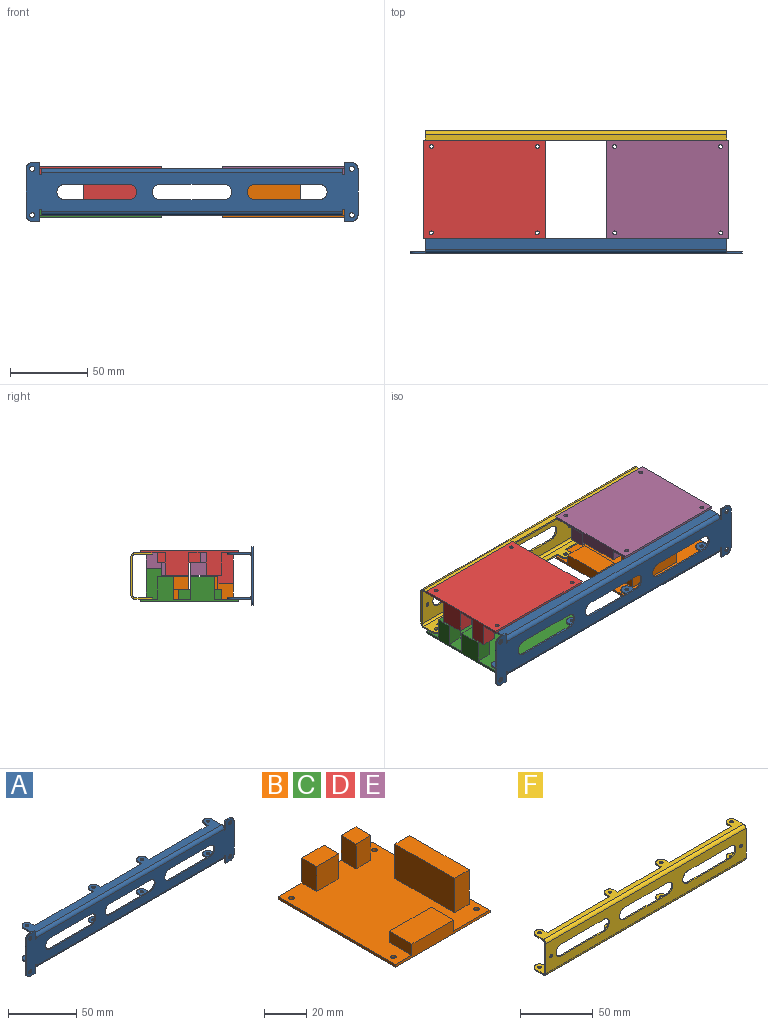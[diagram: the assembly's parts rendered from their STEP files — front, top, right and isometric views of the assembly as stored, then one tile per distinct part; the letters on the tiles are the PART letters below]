
ASSEMBLY  parts=6 mates=5
PART A: 90 faces, bbox 214.8x16.8x38 mm
  f0: plane 214.76x38mm, normal (0,-1,0), area 4067.3mm2, adj f2,f3,f4,f5,f6,f7,f8,f9
  f1: plane 214.76x38mm, normal (0,1,0), area 4067.3mm2, adj f2,f3,f4,f5,f6,f7,f8,f9
  f2: plane 41.59x1mm, normal (0,0,1), area 41.6mm2, adj f0,f1,f29,f31
  f3: plane 41.59x1mm, normal (0,0,-1), area 41.6mm2, adj f0,f1,f24,f30
  f4: plane 7.25x1mm, normal (-1,0,0), area 7.2mm2, adj f0,f1,f5,f34
  f5: plane 4.94x1mm, normal (0,0,-1), area 4.9mm2, adj f0,f1,f4,f25
  f6: plane 30x1mm, normal (1,0,0), area 30mm2, adj f0,f1,f22,f25
  f7: plane 4.94x1mm, normal (0,0,1), area 4.9mm2, adj f0,f1,f8,f22
  f8: plane 7.25x1mm, normal (-1,0,0), area 7.2mm2, adj f0,f1,f7,f37
  f9: plane 7.25x1mm, normal (1,0,0), area 7.2mm2, adj f0,f1,f10,f38
  f10: plane 4.94x1mm, normal (0,0,1), area 4.9mm2, adj f0,f1,f9,f27
  f11: plane 30x1mm, normal (-1,0,0), area 30mm2, adj f0,f1,f26,f27
  f12: plane 4.94x1mm, normal (0,0,-1), area 4.9mm2, adj f0,f1,f19,f26
  f13: plane 41.59x1mm, normal (0,0,-1), area 41.6mm2, adj f0,f1,f23,f28
  f14: plane 41.59x1mm, normal (0,0,1), area 41.6mm2, adj f0,f1,f23,f28
  f15: cylinder r=1.6mm len=3.2mm, axis (0,1,0), area 10.1mm2, adj f0,f1
  f16: cylinder r=1.6mm len=3.2mm, axis (0,1,0), area 10.1mm2, adj f0,f1
  f17: cylinder r=1.6mm len=3.2mm, axis (0,1,0), area 10.1mm2, adj f0,f1
  f18: cylinder r=1.6mm len=3.2mm, axis (0,1,0), area 10.1mm2, adj f0,f1
  f19: plane 7.25x1mm, normal (1,0,0), area 7.2mm2, adj f0,f1,f12,f33
  f20: plane 41.59x1mm, normal (0,0,1), area 41.6mm2, adj f0,f1,f24,f30
  f21: plane 41.59x1mm, normal (0,0,-1), area 41.6mm2, adj f0,f1,f29,f31
  f22: cylinder r=4mm len=4mm, axis (0,-1,0), area 6.3mm2, adj f0,f1,f6,f7
  f23: cylinder r=5mm len=10mm, axis (0,1,0), area 15.7mm2, adj f0,f1,f13,f14
  f24: cylinder r=5mm len=10mm, axis (0,-1,0), area 15.7mm2, adj f0,f1,f3,f20
  f25: cylinder r=4mm len=4mm, axis (0,1,0), area 6.3mm2, adj f0,f1,f5,f6
  f26: cylinder r=4mm len=4mm, axis (0,1,0), area 6.3mm2, adj f0,f1,f11,f12
  f27: cylinder r=4mm len=4mm, axis (0,-1,0), area 6.3mm2, adj f0,f1,f10,f11
  f28: cylinder r=5mm len=10mm, axis (0,1,0), area 15.7mm2, adj f0,f1,f13,f14
  f29: cylinder r=5mm len=10mm, axis (0,-1,0), area 15.7mm2, adj f0,f1,f2,f21
  f30: cylinder r=5mm len=10mm, axis (0,1,0), area 15.7mm2, adj f0,f1,f3,f20
  f31: cylinder r=5mm len=10mm, axis (0,-1,0), area 15.7mm2, adj f0,f1,f2,f21
  f32: plane 1x0.75mm, normal (-1,0,0), area 0.7mm2, adj f0,f1,f33,f62
  f33: cylinder r=0.53mm len=1.06mm, axis (0,1,0), area 1.7mm2, adj f0,f1,f19,f32
  f34: cylinder r=0.53mm len=1.06mm, axis (0,1,0), area 1.7mm2, adj f0,f1,f4,f35
  f35: plane 1x0.75mm, normal (1,0,0), area 0.7mm2, adj f0,f1,f34,f61
  f36: plane 1x0.75mm, normal (1,0,0), area 0.7mm2, adj f0,f1,f37,f86
  f37: cylinder r=0.53mm len=1.06mm, axis (0,1,0), area 1.7mm2, adj f0,f1,f8,f36
  f38: cylinder r=0.53mm len=1.06mm, axis (0,1,0), area 1.7mm2, adj f0,f1,f9,f39
  f39: plane 1x0.75mm, normal (-1,0,0), area 0.7mm2, adj f0,f1,f38,f87
  f40: cylinder r=3.8mm len=7.6mm, axis (0,0,-1), area 11.9mm2, adj f41,f58,f59,f60
  f41: plane 3.8x1mm, normal (1,0,0), area 3.8mm2, adj f40,f42,f59,f60
  f42: plane 60.98x1mm, normal (0,1,0), area 61mm2, adj f41,f43,f59,f60
  f43: plane 3.8x1mm, normal (-1,0,0), area 3.8mm2, adj f42,f44,f59,f60
  f44: cylinder r=3.8mm len=7.6mm, axis (0,0,-1), area 11.9mm2, adj f43,f45,f59,f60
  f45: plane 3.8x1mm, normal (1,0,0), area 3.8mm2, adj f44,f46,f59,f60
  f46: plane 42.4x1mm, normal (0,1,0), area 42.4mm2, adj f45,f47,f59,f60
  f47: plane 3.8x1mm, normal (-1,0,0), area 3.8mm2, adj f46,f48,f59,f60
  f48: cylinder r=3.8mm len=7.6mm, axis (0,0,-1), area 11.9mm2, adj f47,f49,f59,f60
  f49: plane 3.8x1mm, normal (1,0,0), area 3.8mm2, adj f48,f50,f59,f60
  f50: plane 60.98x1mm, normal (0,1,0), area 61mm2, adj f49,f51,f59,f60
  f51: plane 3.8x1mm, normal (-1,0,0), area 3.8mm2, adj f50,f52,f59,f60
  f52: cylinder r=3.8mm len=7.6mm, axis (0,0,-1), area 11.9mm2, adj f51,f53,f59,f60
  f53: plane 10.5x1mm, normal (1,0,0), area 10.5mm2, adj f52,f59,f60,f61
  f54: cylinder r=1.25mm len=2.5mm, axis (0,0,-1), area 7.9mm2, adj f59,f60
  f55: cylinder r=1.25mm len=2.5mm, axis (0,0,-1), area 7.9mm2, adj f59,f60
  f56: cylinder r=1.25mm len=2.5mm, axis (0,0,-1), area 7.9mm2, adj f59,f60
  f57: cylinder r=1.25mm len=2.5mm, axis (0,0,-1), area 7.9mm2, adj f59,f60
  f58: plane 10.5x1mm, normal (-1,0,0), area 10.5mm2, adj f40,f59,f60,f62
  f59: plane 194.76x14.3mm, normal (0,0,-1), area 1491.5mm2, adj f40,f41,f42,f43,f44,f45,f46,f47
  f60: plane 194.76x14.3mm, normal (0,0,1), area 1491.5mm2, adj f40,f41,f42,f43,f44,f45,f46,f47
  f61: plane 2.5x2.5mm, normal (1,0,0), area 3.1mm2, adj f35,f53,f63,f64
  f62: plane 2.5x2.5mm, normal (-1,0,0), area 3.1mm2, adj f32,f58,f63,f64
  f63: cylinder r=2.5mm len=194.76mm, axis (1,0,0), area 764.8mm2, adj f0,f59,f61,f62
  f64: cylinder r=1.5mm len=194.76mm, axis (1,0,0), area 458.9mm2, adj f1,f60,f61,f62
  f65: cylinder r=3.8mm len=7.6mm, axis (0,0,1), area 11.9mm2, adj f66,f83,f84,f85
  f66: plane 3.8x1mm, normal (-1,0,0), area 3.8mm2, adj f65,f67,f84,f85
  f67: plane 60.98x1mm, normal (0,1,0), area 61mm2, adj f66,f68,f84,f85
  f68: plane 3.8x1mm, normal (1,0,0), area 3.8mm2, adj f67,f69,f84,f85
  f69: cylinder r=3.8mm len=7.6mm, axis (0,0,1), area 11.9mm2, adj f68,f70,f84,f85
  f70: plane 3.8x1mm, normal (-1,0,0), area 3.8mm2, adj f69,f71,f84,f85
  f71: plane 42.4x1mm, normal (0,1,0), area 42.4mm2, adj f70,f72,f84,f85
  f72: plane 3.8x1mm, normal (1,0,0), area 3.8mm2, adj f71,f73,f84,f85
  f73: cylinder r=3.8mm len=7.6mm, axis (0,0,1), area 11.9mm2, adj f72,f74,f84,f85
  f74: plane 3.8x1mm, normal (-1,0,0), area 3.8mm2, adj f73,f75,f84,f85
  f75: plane 60.98x1mm, normal (0,1,0), area 61mm2, adj f74,f76,f84,f85
  f76: plane 3.8x1mm, normal (1,0,0), area 3.8mm2, adj f75,f77,f84,f85
  f77: cylinder r=3.8mm len=7.6mm, axis (0,0,1), area 11.9mm2, adj f76,f78,f84,f85
  f78: plane 10.5x1mm, normal (-1,0,0), area 10.5mm2, adj f77,f84,f85,f87
  f79: cylinder r=1.25mm len=2.5mm, axis (0,0,1), area 7.9mm2, adj f84,f85
  f80: cylinder r=1.25mm len=2.5mm, axis (0,0,1), area 7.9mm2, adj f84,f85
  f81: cylinder r=1.25mm len=2.5mm, axis (0,0,1), area 7.9mm2, adj f84,f85
  f82: cylinder r=1.25mm len=2.5mm, axis (0,0,1), area 7.9mm2, adj f84,f85
  f83: plane 10.5x1mm, normal (1,0,0), area 10.5mm2, adj f65,f84,f85,f86
  f84: plane 194.76x14.3mm, normal (0,0,1), area 1491.5mm2, adj f65,f66,f67,f68,f69,f70,f71,f72
  f85: plane 194.76x14.3mm, normal (0,0,-1), area 1491.5mm2, adj f65,f66,f67,f68,f69,f70,f71,f72
  f86: plane 2.5x2.5mm, normal (1,0,0), area 3.1mm2, adj f36,f83,f88,f89
  f87: plane 2.5x2.5mm, normal (-1,0,0), area 3.1mm2, adj f39,f78,f88,f89
  f88: cylinder r=2.5mm len=194.76mm, axis (1,0,0), area 764.8mm2, adj f0,f84,f86,f87
  f89: cylinder r=1.5mm len=194.76mm, axis (1,0,0), area 458.9mm2, adj f1,f85,f86,f87
PART B: 27 faces, bbox 63.5x79.1x21.5 mm
  f0: plane 79.12x63.5mm, normal (0,0,1), area 3934.5mm2, adj f1,f2,f3,f4,f6,f7,f8,f9
  f1: plane 63.5x8mm, normal (0,-1,0), area 277.3mm2, adj f0,f2,f4,f5,f23,f24,f26
  f2: plane 79.12x1.5mm, normal (1,0,0), area 118.7mm2, adj f0,f1,f3,f5
  f3: plane 63.5x16mm, normal (0,1,0), area 457.7mm2, adj f0,f2,f4,f5,f10,f12,f13,f14
  f4: plane 79.12x1.5mm, normal (-1,0,0), area 118.7mm2, adj f0,f1,f3,f5
  f5: plane 79.12x63.5mm, normal (0,0,-1), area 5004.5mm2, adj f1,f2,f3,f4,f6,f7,f8,f9
  f6: cylinder r=1.25mm len=2.5mm, axis (0,0,1), area 11.8mm2, adj f0,f5
  f7: cylinder r=1.25mm len=2.5mm, axis (0,0,1), area 11.8mm2, adj f0,f5
  f8: cylinder r=1.25mm len=2.5mm, axis (0,0,1), area 11.8mm2, adj f0,f5
  f9: cylinder r=1.25mm len=2.5mm, axis (0,0,1), area 11.8mm2, adj f0,f5
  f10: plane 14.5x10mm, normal (-1,0,0), area 145mm2, adj f0,f3,f11,f13
  f11: plane 15x14.5mm, normal (0,-1,0), area 217.5mm2, adj f0,f10,f12,f13
  f12: plane 14.5x10mm, normal (1,0,0), area 145mm2, adj f0,f3,f11,f13
  f13: plane 15x10mm, normal (0,0,1), area 150mm2, adj f3,f10,f11,f12
  f14: plane 14.5x10mm, normal (1,0,0), area 145mm2, adj f0,f3,f16,f17
  f15: plane 14.5x10mm, normal (-1,0,0), area 145mm2, adj f0,f3,f16,f17
  f16: plane 14.5x10mm, normal (0,-1,0), area 145mm2, adj f0,f14,f15,f17
  f17: plane 10x10mm, normal (0,0,1), area 100mm2, adj f3,f14,f15,f16
  f18: plane 20x10mm, normal (0,1,0), area 200mm2, adj f0,f19,f21,f22
  f19: plane 40x20mm, normal (-1,0,0), area 800mm2, adj f0,f18,f20,f22
  f20: plane 20x10mm, normal (0,-1,0), area 200mm2, adj f0,f19,f21,f22
  f21: plane 40x20mm, normal (1,0,0), area 800mm2, adj f0,f18,f20,f22
  f22: plane 40x10mm, normal (0,0,1), area 400mm2, adj f18,f19,f20,f21
  f23: plane 15x6.5mm, normal (-1,0,0), area 97.5mm2, adj f0,f1,f25,f26
  f24: plane 15x6.5mm, normal (1,0,0), area 97.5mm2, adj f0,f1,f25,f26
  f25: plane 28x6.5mm, normal (0,1,0), area 182mm2, adj f0,f23,f24,f26
  f26: plane 28x15mm, normal (0,0,1), area 420mm2, adj f1,f23,f24,f25
PART C: same geometry as B
PART D: same geometry as B
PART E: same geometry as B
PART F: 68 faces, bbox 194.8x13.9x30 mm
  f0: plane 41.59x1mm, normal (0,0,1), area 41.6mm2, adj f10,f11,f13,f17
  f1: plane 41.59x1mm, normal (0,0,-1), area 41.6mm2, adj f10,f11,f12,f16
  f2: plane 25x1mm, normal (-1,0,0), area 25mm2, adj f10,f11,f40,f65
  f3: plane 41.59x1mm, normal (0,0,-1), area 41.6mm2, adj f10,f11,f14,f15
  f4: plane 41.59x1mm, normal (0,0,1), area 41.6mm2, adj f10,f11,f14,f15
  f5: cylinder r=1.25mm len=2.5mm, axis (0,1,0), area 7.9mm2, adj f10,f11
  f6: cylinder r=1.25mm len=2.5mm, axis (0,1,0), area 7.9mm2, adj f10,f11
  f7: plane 25x1mm, normal (1,0,0), area 25mm2, adj f10,f11,f39,f64
  f8: plane 41.59x1mm, normal (0,0,1), area 41.6mm2, adj f10,f11,f12,f16
  f9: plane 41.59x1mm, normal (0,0,-1), area 41.6mm2, adj f10,f11,f13,f17
  f10: plane 194.76x25mm, normal (0,-1,0), area 3376mm2, adj f0,f1,f2,f3,f4,f5,f6,f7
  f11: plane 194.76x25mm, normal (0,1,0), area 3376mm2, adj f0,f1,f2,f3,f4,f5,f6,f7
  f12: cylinder r=5mm len=10mm, axis (0,-1,0), area 15.7mm2, adj f1,f8,f10,f11
  f13: cylinder r=5mm len=10mm, axis (0,-1,0), area 15.7mm2, adj f0,f9,f10,f11
  f14: cylinder r=5mm len=10mm, axis (0,-1,0), area 15.7mm2, adj f3,f4,f10,f11
  f15: cylinder r=5mm len=10mm, axis (0,-1,0), area 15.7mm2, adj f3,f4,f10,f11
  f16: cylinder r=5mm len=10mm, axis (0,-1,0), area 15.7mm2, adj f1,f8,f10,f11
  f17: cylinder r=5mm len=10mm, axis (0,1,0), area 15.7mm2, adj f0,f9,f10,f11
  f18: cylinder r=3.8mm len=7.6mm, axis (0,0,-1), area 11.9mm2, adj f19,f36,f37,f38
  f19: plane 3.8x1mm, normal (1,0,0), area 3.8mm2, adj f18,f20,f37,f38
  f20: plane 60.98x1mm, normal (0,1,0), area 61mm2, adj f19,f21,f37,f38
  f21: plane 3.8x1mm, normal (-1,0,0), area 3.8mm2, adj f20,f22,f37,f38
  f22: cylinder r=3.8mm len=7.6mm, axis (0,0,-1), area 11.9mm2, adj f21,f23,f37,f38
  f23: plane 3.8x1mm, normal (1,0,0), area 3.8mm2, adj f22,f24,f37,f38
  f24: plane 42.4x1mm, normal (0,1,0), area 42.4mm2, adj f23,f25,f37,f38
  f25: plane 3.8x1mm, normal (-1,0,0), area 3.8mm2, adj f24,f26,f37,f38
  f26: cylinder r=3.8mm len=7.6mm, axis (0,0,-1), area 11.9mm2, adj f25,f27,f37,f38
  f27: plane 3.8x1mm, normal (1,0,0), area 3.8mm2, adj f26,f28,f37,f38
  f28: plane 60.98x1mm, normal (0,1,0), area 61mm2, adj f27,f29,f37,f38
  f29: plane 3.8x1mm, normal (-1,0,0), area 3.8mm2, adj f28,f30,f37,f38
  f30: cylinder r=3.8mm len=7.6mm, axis (0,0,-1), area 11.9mm2, adj f29,f31,f37,f38
  f31: plane 7.62x1mm, normal (1,0,0), area 7.6mm2, adj f30,f37,f38,f39
  f32: cylinder r=1.25mm len=2.5mm, axis (0,0,-1), area 7.9mm2, adj f37,f38
  f33: cylinder r=1.25mm len=2.5mm, axis (0,0,-1), area 7.9mm2, adj f37,f38
  f34: cylinder r=1.25mm len=2.5mm, axis (0,0,-1), area 7.9mm2, adj f37,f38
  f35: cylinder r=1.25mm len=2.5mm, axis (0,0,-1), area 7.9mm2, adj f37,f38
  f36: plane 7.62x1mm, normal (-1,0,0), area 7.6mm2, adj f18,f37,f38,f40
  f37: plane 194.76x11.42mm, normal (0,0,-1), area 930.6mm2, adj f18,f19,f20,f21,f22,f23,f24,f25
  f38: plane 194.76x11.42mm, normal (0,0,1), area 930.6mm2, adj f18,f19,f20,f21,f22,f23,f24,f25
  f39: plane 2.5x2.5mm, normal (1,0,0), area 3.1mm2, adj f7,f31,f41,f42
  f40: plane 2.5x2.5mm, normal (-1,0,0), area 3.1mm2, adj f2,f36,f41,f42
  f41: cylinder r=2.5mm len=194.76mm, axis (1,0,0), area 764.8mm2, adj f10,f37,f39,f40
  f42: cylinder r=1.5mm len=194.76mm, axis (1,0,0), area 458.9mm2, adj f11,f38,f39,f40
  f43: cylinder r=3.8mm len=7.6mm, axis (0,0,1), area 11.9mm2, adj f44,f61,f62,f63
  f44: plane 3.8x1mm, normal (-1,0,0), area 3.8mm2, adj f43,f45,f62,f63
  f45: plane 60.98x1mm, normal (0,1,0), area 61mm2, adj f44,f46,f62,f63
  f46: plane 3.8x1mm, normal (1,0,0), area 3.8mm2, adj f45,f47,f62,f63
  f47: cylinder r=3.8mm len=7.6mm, axis (0,0,1), area 11.9mm2, adj f46,f48,f62,f63
  f48: plane 3.8x1mm, normal (-1,0,0), area 3.8mm2, adj f47,f49,f62,f63
  f49: plane 42.4x1mm, normal (0,1,0), area 42.4mm2, adj f48,f50,f62,f63
  f50: plane 3.8x1mm, normal (1,0,0), area 3.8mm2, adj f49,f51,f62,f63
  f51: cylinder r=3.8mm len=7.6mm, axis (0,0,1), area 11.9mm2, adj f50,f52,f62,f63
  f52: plane 3.8x1mm, normal (-1,0,0), area 3.8mm2, adj f51,f53,f62,f63
  f53: plane 60.98x1mm, normal (0,1,0), area 61mm2, adj f52,f54,f62,f63
  f54: plane 3.8x1mm, normal (1,0,0), area 3.8mm2, adj f53,f55,f62,f63
  f55: cylinder r=3.8mm len=7.6mm, axis (0,0,1), area 11.9mm2, adj f54,f56,f62,f63
  f56: plane 7.62x1mm, normal (-1,0,0), area 7.6mm2, adj f55,f62,f63,f65
  f57: cylinder r=1.25mm len=2.5mm, axis (0,0,1), area 7.9mm2, adj f62,f63
  f58: cylinder r=1.25mm len=2.5mm, axis (0,0,1), area 7.9mm2, adj f62,f63
  f59: cylinder r=1.25mm len=2.5mm, axis (0,0,1), area 7.9mm2, adj f62,f63
  f60: cylinder r=1.25mm len=2.5mm, axis (0,0,1), area 7.9mm2, adj f62,f63
  f61: plane 7.62x1mm, normal (1,0,0), area 7.6mm2, adj f43,f62,f63,f64
  f62: plane 194.76x11.42mm, normal (0,0,1), area 930.6mm2, adj f43,f44,f45,f46,f47,f48,f49,f50
  f63: plane 194.76x11.42mm, normal (0,0,-1), area 930.6mm2, adj f43,f44,f45,f46,f47,f48,f49,f50
  f64: plane 2.5x2.5mm, normal (1,0,0), area 3.1mm2, adj f7,f61,f66,f67
  f65: plane 2.5x2.5mm, normal (-1,0,0), area 3.1mm2, adj f2,f56,f66,f67
  f66: cylinder r=2.5mm len=194.76mm, axis (1,0,0), area 764.8mm2, adj f10,f62,f64,f65
  f67: cylinder r=1.5mm len=194.76mm, axis (1,0,0), area 458.9mm2, adj f11,f63,f64,f65
PLACE A at identity
PLACE B rot(axis=(0,0,-1),90deg) t=(59.29,0,20)mm
PLACE C rot(axis=(0,0,1),90deg) t=(-59.29,0,20)mm
PLACE D rot(axis=(-0.71,0.71,0),180deg) t=(-59.29,0,50)mm
PLACE E rot(axis=(-0.71,-0.71,0),180deg) t=(59.29,0,50)mm
PLACE F rot(axis=(0,0,1),180deg) t=(0,0,0)mm
MATE fastened B.f7 <-> A.f52  axis (0,0,1) through (93.58,-27.94,20)mm
MATE fastened A.f77 <-> D.f7  axis (0,0,1) through (-93.58,-27.94,50)mm
MATE fastened E.f6 <-> A.f65  axis (0,0,-1) through (93.58,-27.94,50)mm
MATE fastened C.f6 <-> A.f40  axis (0,0,1) through (-93.58,-27.94,20)mm
MATE fastened F.f30 <-> C.f7  axis (0,0,-1) through (-93.58,27.94,20)mm
